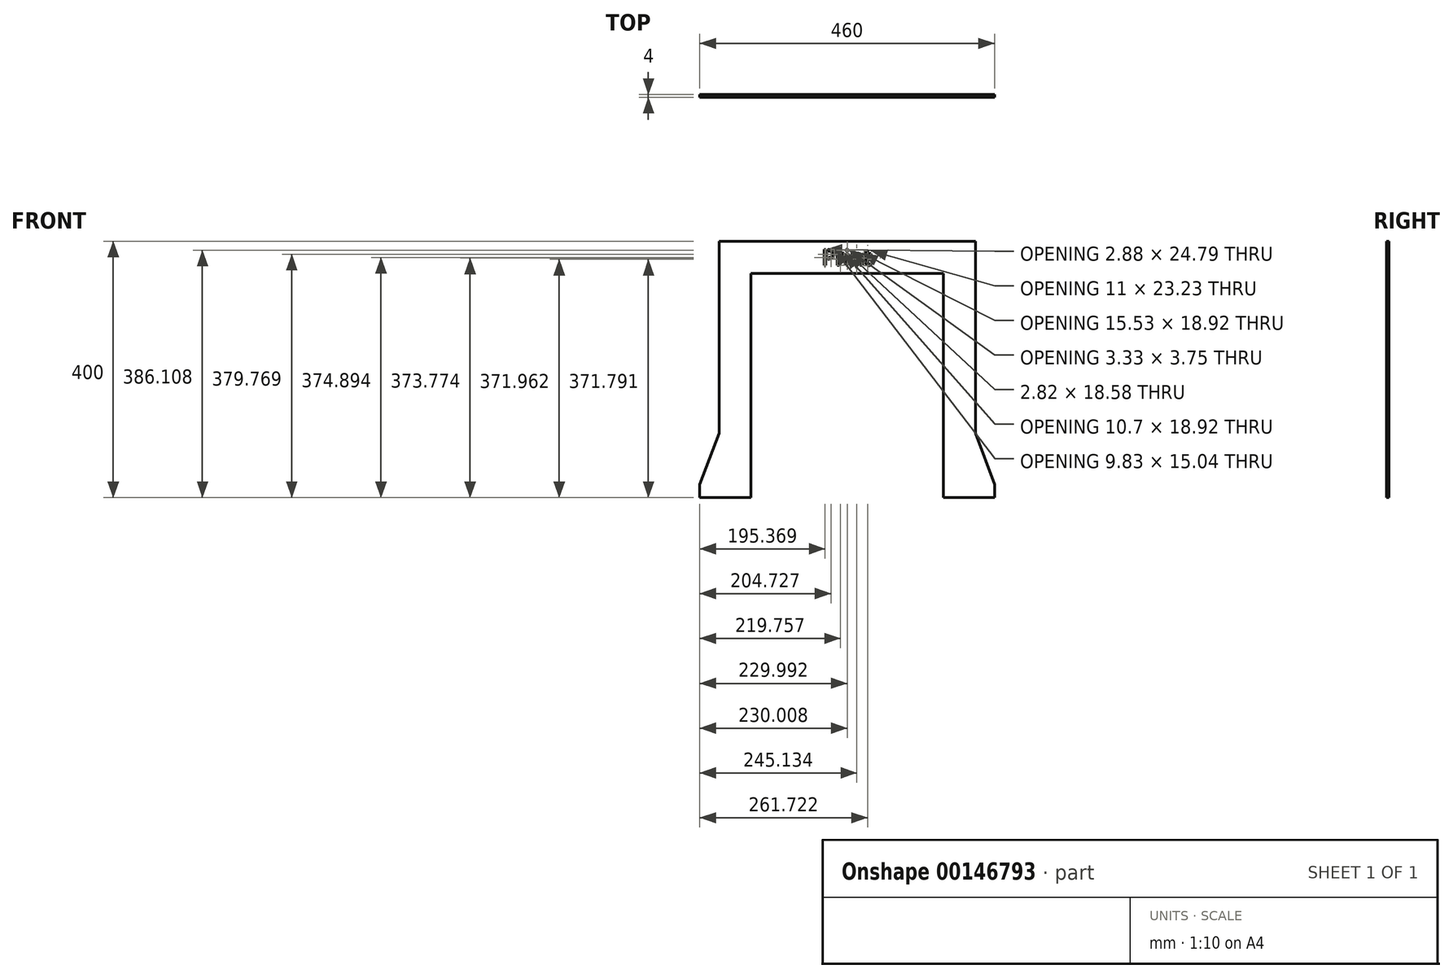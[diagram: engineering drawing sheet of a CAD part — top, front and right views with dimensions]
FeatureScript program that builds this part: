
annotation { "Feature Type Name" : "Feature", "Feature Type Description" : "" }
export const myFeature = defineFeature(function(context is Context, id is Id, definition is map)
    precondition{}
    {
        {
            var Q0;
            Q0=qCreatedBy(makeId("Front.planeOp"),FACE);
            var sketch = newSketch(context, id + "F0", { "sketchPlane" : qUnion([Q0])});
            skLineSegment(sketch, "E0", {"start": v(-150, 0) * mm, "end": v(150, 0) * mm});
            skLineSegment(sketch, "E1", {"start": v(-150, 0) * mm, "end": v(-150, -350) * mm});
            skLineSegment(sketch, "E2", {"start": v(150, 0) * mm, "end": v(150, -350) * mm});
            skLineSegment(sketch, "E3", {"start": v(-150, -350) * mm, "end": v(-230, -350) * mm});
            skLineSegment(sketch, "E4", {"start": v(-200, -250) * mm, "end": v(-200, 50) * mm});
            skLineSegment(sketch, "E5", {"start": v(-200, 50) * mm, "end": v(200, 50) * mm});
            skLineSegment(sketch, "E6", {"start": v(200, 50) * mm, "end": v(200, -250) * mm});
            skLineSegment(sketch, "E7", {"start": v(230, -350) * mm, "end": v(150, -350) * mm});
            skLineSegment(sketch, "E8", {"start": v(-200, -250) * mm, "end": v(-230, -330) * mm});
            skLineSegment(sketch, "E9", {"start": v(200, -250) * mm, "end": v(230, -330) * mm});
            skLineSegment(sketch, "E10", {"start": v(-230, -350) * mm, "end": v(-230, -330) * mm});
            skLineSegment(sketch, "E11", {"start": v(230, -350) * mm, "end": v(230, -330) * mm});
            skSolve(sketch);
        }
        {
            var Q0;
            Q0 = qSketchRegion(id + "F0", true);
            extrude(context, id + "F1", {"entities" : qUnion([Q0]), "depth" : 4 * mm});
        }
        {
            var Q0;
            Q0=makeQuery(id+"F1.opExtrude","CAP_FACE",FACE,{"disambiguationData":[OSD([sQuery(id+"F0.wireOp",EDGE,"E0"),sQuery(id+"F0.wireOp",EDGE,"E1"),sQuery(id+"F0.wireOp",EDGE,"E2"),sQuery(id+"F0.wireOp",EDGE,"E3"),sQuery(id+"F0.wireOp",EDGE,"E4"),sQuery(id+"F0.wireOp",EDGE,"E5"),sQuery(id+"F0.wireOp",EDGE,"E6"),sQuery(id+"F0.wireOp",EDGE,"E7")])],"isStart":false});
            var sketch = newSketch(context, id + "F2", { "sketchPlane" : qUnion([Q0])});
            skText(sketch, "E12", { "text": "Print", "fontName": "OpenSans-Regular.ttf"});
            skLineSegment(sketch, "E13", {"start": v(0, 50) * mm, "end": v(0, 37.5) * mm, "construction": true});
            skLineSegment(sketch, "E14", {"start": v(0, 12.5) * mm, "end": v(0, 0) * mm, "construction": true});
            const initialGuessF2  = {"E12": [-0.03948, 0.0125, 1, 0, 0.025]};
            skSetInitialGuess(sketch, initialGuessF2);
            skSolve(sketch);
        }
        {
            var Q0;
            Q0 = qSketchRegion(id + "F2", true);
            extrude(context, id + "F3", {"entities" : qUnion([Q0]), "operationType" : NewBodyOperationType.REMOVE, "oppositeDirection" : true, "depth" : 25 * mm});
        }
        {
            var Q0;
            {var subQ0=sQuery(id+"F0.wireOp",EDGE,"E7");var subQ1=sQuery(id+"F0.wireOp",EDGE,"E6");var subQ2=sQuery(id+"F0.wireOp",EDGE,"E4");var subQ3=sQuery(id+"F0.wireOp",EDGE,"E5");var subQ4=sQuery(id+"F0.wireOp",EDGE,"E1");var subQ5=sQuery(id+"F0.wireOp",EDGE,"E2");var subQ6=sQuery(id+"F0.wireOp",EDGE,"E3");var subQ7=sQuery(id+"F0.wireOp",EDGE,"E0");Q0=makeQuery(id+"F3.boolean.opBoolean","SPLIT",FACE,{"disambiguationData":[TD([makeQuery(id+"F1.opExtrude","SWEPT_FACE",FACE,{"disambiguationData":[OSD([subQ7])]})])],"derivedFrom":makeQuery(id+"F1.opExtrude","CAP_FACE",FACE,{"disambiguationData":[OSD([subQ7,subQ4,subQ5,subQ6,subQ2,subQ3,subQ1,subQ0])],"isStart":false})});}
            var sketch = newSketch(context, id + "F4", { "sketchPlane" : qUnion([Q0])});
            skLineSegment(sketch, "E15", {"start": v(-33.19, 22.25) * mm, "end": v(-33.19, 37.29) * mm});
            skLineSegment(sketch, "E16", {"start": v(-33.19, 37.29) * mm, "end": v(-30.19, 37.29) * mm});
            skLineSegment(sketch, "E17", {"start": v(-30.19, 37.29) * mm, "end": v(-30.19, 22.25) * mm});
            skLineSegment(sketch, "E18", {"start": v(-30.19, 22.25) * mm, "end": v(-33.19, 22.25) * mm});
            skSolve(sketch);
        }
        {
            var Q0;
            Q0 = qSketchRegion(id + "F4", true);
            extrude(context, id + "F5", {"entities" : qUnion([Q0]), "operationType" : NewBodyOperationType.ADD, "oppositeDirection" : true, "depth" : 4 * mm});
        }
    });
